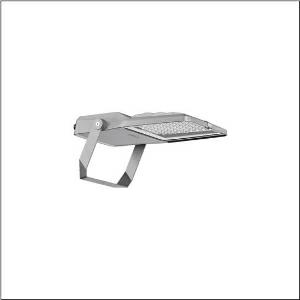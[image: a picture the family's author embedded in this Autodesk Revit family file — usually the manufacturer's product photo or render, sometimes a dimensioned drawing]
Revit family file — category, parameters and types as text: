
# Revit family: floodlight_fl_21_iq_mini___pl52_5xa7772d5d1a_a443
name_source: partatom
category: Lighting Fixtures
units: mm (PartAtom-declared; Revit-internal decimal feet)

## family parameters
Cut with Voids When Loaded = No
Host = Face
Light Source = No
Part Type = Normal
Room Calculation Point = No
Round Connector Dimension = Use Diameter
Shared = No

## types (1)
- --- (1 x LED, 16640 lm, 143 W, 4000K)
    Apparent Load = 143 VA
    CIE Flux Codes = 26 60 98 100 100
    Color Rendering = 80
    Color Temperature = 4000K
    Default Elevation = 1800 mm
    Description = Floodlight FL 21 iQ mini, floodlight, primary light control with lens, of PMMA, primary optical cover: protective disc, of toughened safety glass, transparent, light distribution: PL52, light emission: direct distribution, installation type: surface-mounted, lamps: LED, High Power LED, rated values: 16.640lm | 143W | 116,4lm/W (begin service life); end service life: 16.640lm | 151,6W; at 50% lumin. flux: 8.320lm | 60,6W | 137,3lm/W, colour temperature: 4000K, colour rendering: CRI > 80, light colour: 840, light setting 1 begin service life: 100% | 16.640lm | 143W | 116,4lm/W | 4.000K, light setting 1 end service life: 151,6W, further light settings possible, control: Street-Remote, Auto-Match, Temp-Guard, Night-Set, Smart-Wire, Desk-Remote (wireless, voltage-free reading and setting of iQ features in the workshop via application-optimized NFC function/RFID function), optimised constant luminous flux control (CLO 2.0), pre-setting: linear dimming characteristic, with terminal, 6-pole, mains connection: 220..240V, AC, 50/60Hz, luminaire housing, of diecast aluminium, powder-coated, SITECO metallic grey (DB 702S), corrosivity category C5 mid according to DIN EN ISO 12944suitable for swimming poolschlorine-resistant, sealing non-destructively replaceable, mounting bracket, of steel, galvanised, powder-coated, SITECO metallic grey (DB 702S), protection rating (complete): IP66, insulation class (complete): insulation class II (safety insulation), certification: CE, ENEC, VDE, protection symbol: D, impact resistance: IK08, permissible operating ambient temperature: -40..+40°C, permissible operating ambient temperature for outdoor applications: -40..+50°C, standard: DIN EN 12944, LABS conformity tested according to VDMA 24364:2018-05, packaging unit: 1 piece

Light Distribution: PL52
    Height = 70 mm
    Lamp = 1 x LED
    Lamp Light Flux = 16640 lm
    Lamp Power = 143 W
    Lamp count = 1
    Length = 485 mm
    Luminous efficacy = 116 lm/W
    Manufacturer = Siteco
    ModVariant = No
    Model = 5XA7772D5D1A
    Number of Poles = 1
    OnlyDefault = Yes
    Power Factor = 1
    Product Name = Floodlight FL 21 iQ mini | PL52
    Product group = floodlight | pylon annexe
    ProductGroupID = 6201
    Protection Class = Protection class II
    Protection Degree = IP 66
    RLX_Detail_Level = 1
    RLX_Emergency_Light_Flux = 0 lm
    RLX_Emergency_Type = 0
    RLX_Emergency_Type_DB = No
    RlxData = <blob elided: 96945 chars, md5=6294323e>
    Socket = socket
    Standby Power = 0 W
    System Light Flux = 16640 lm
    System Power = 143 W
    Type Comments = factory setting: luminous flux: 100 % | dim-lin: 254 | 730 mA
    Type Image = l_1006845.jpg
    URL = http://relux.com
    VarID = @adj_162991
    Voltage = 0 V
    Weight = 0.00 kg
    Width = 337 mm

## geometry (parser evidence)
native form markers: Blend x4, Sweep x12
no freeform markers — native parametric forms only
